# Revit family: 510100 SMART COMMAND ISOLATION VALVE DN20
name_source: partatom
category: Plumbing Fixtures
revit_build: Autodesk Revit 2016 (Build: 20161004_0715(x64)
units: mm (PartAtom-declared; Revit-internal decimal feet)

## family parameters
Cut with Voids When Loaded = No
Host = Face
OmniClass Number = 23.45.55.11
OmniClass Title = Sanitary Components
Part Type = Normal
Room Calculation Point = No
Round Connector Dimension = Use Radius
Shared = No

## types (1)
- SMART COMMAND ISOLATION VALVE DN20
    Assembly Code = C1030210
    CW Connection = Yes
    Default Elevation = 900 mm  [stored 2.95276 ft]
    Description = SMART COMMAND ISOLATION VALVE DN20
    HW Connection = No
    Manufacturer = GWA Bathrooms & Kitchens
    Material_Base = GWA-Metal-White
    Material_Connection = GWA_Metal-Chrome
    Material_Cover = GWA-Acrylic-Smoke
    Model = 510100
    URL = https://www.caroma.com.au
    Vent Connection = No
    Waste Connection = No

note: [stored X ft] marks values corroborated as IEEE doubles in the binary element streams (Revit-internal decimal feet)

## geometry (parser evidence)
native form markers: Sweep x2
no freeform markers — native parametric forms only
